# Revit family: Exterior Swing
name_source: partatom
category: Doors
revit_build: Autodesk Revit LT 2013 (Build: 20120821_1330(x64)
units: mm (PartAtom-declared; Revit-internal decimal feet)

## types (1)
- Exterior Swing
    Door Swing Angle = 89.00°
    Door Thickness = 0' - 1 1/2"
    Door Type = Full Lite
    Ext Trim = <By Category>
    Exterior Door Finish = <By Category>
    Exterior Frame Finish = <By Category>
    Exterior Trim = Yes
    Exterior Wrap Depth = 0' - 0 1/2"
    Frame Thickness = 0' - 1"
    Function = Exterior
    Glass = <By Category>
    Height = 7' - 0"
    Int Trim = <By Category>
    Interior Door Finish = <By Category>
    Interior Frame Finish = <By Category>
    Interior Trim = Yes
    Interior Wrap Depth = 0' - 1"
    Rough Height = 7' - 2"
    Rough Width = 3' - 2"
    Sill = <By Category>
    Sill Ear Length = 0' - 1 1/2"
    Sill Projection = 0' - 1 1/2"
    Sill Thickness = 0' - 1"
    Thickness = 1' - 0"
    Trim Projection Ext. = 0' - 1"
    Trim Projection Int. = 0' - 1"
    Trim Width = 0' - 3"
    Wall Closure = Both
    Width = 3' - 0"

## geometry (parser evidence)
native form markers: Sweep x14
no freeform markers — native parametric forms only
